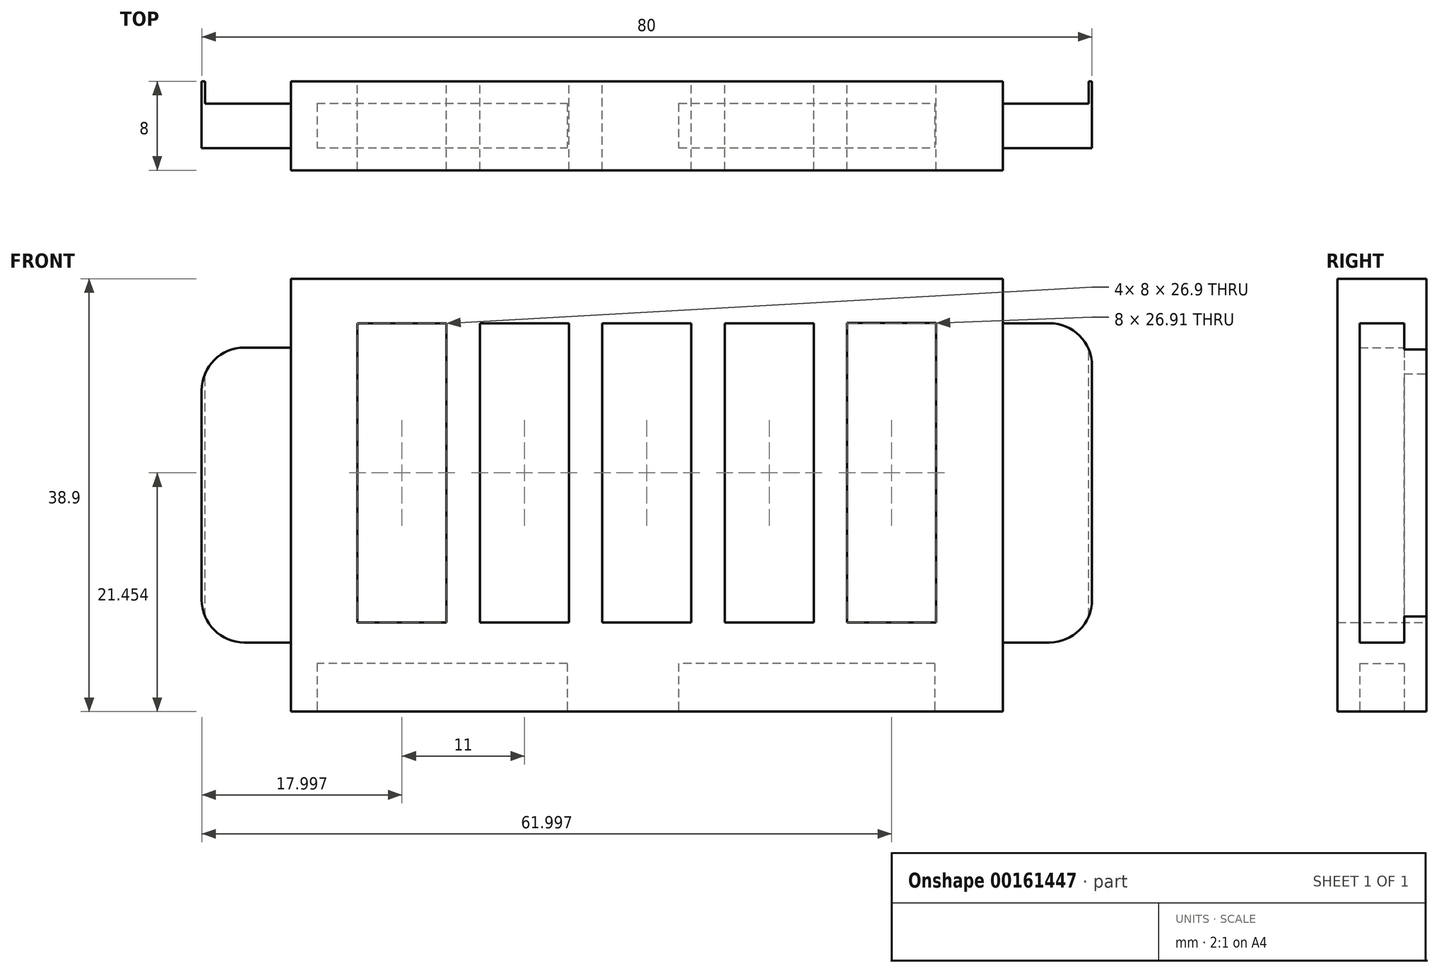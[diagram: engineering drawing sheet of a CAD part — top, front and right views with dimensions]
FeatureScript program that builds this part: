
annotation { "Feature Type Name" : "Feature", "Feature Type Description" : "" }
export const myFeature = defineFeature(function(context is Context, id is Id, definition is map)
    precondition{}
    {
        {
            var Q0;
            Q0=qCreatedBy(makeId("Front.planeOp"),FACE);
            var sketch = newSketch(context, id + "F0", { "sketchPlane" : qUnion([Q0])});
            skLineSegment(sketch, "E0.bottom", {"start": v(-77.72, 39.57) * mm, "end": v(-71.72, 39.57) * mm});
            skLineSegment(sketch, "E0.left", {"start": v(-77.72, 39.57) * mm, "end": v(-77.72, 0.67) * mm});
            skLineSegment(sketch, "E0.right", {"start": v(-13.72, 39.57) * mm, "end": v(-13.72, 0.67) * mm});
            skLineSegment(sketch, "E1.left", {"start": v(-77.72, 0.67) * mm, "end": v(-77.72, 15.56) * mm});
            skLineSegment(sketch, "E1.right", {"start": v(-85.72, 10.7) * mm, "end": v(-85.72, 29.54) * mm});
            skLineSegment(sketch, "E2.top", {"start": v(-77.72, 6.87) * mm, "end": v(-81.89, 6.87) * mm});
            skLineSegment(sketch, "E2.left", {"start": v(-77.72, 0.67) * mm, "end": v(-77.72, 6.87) * mm});
            skLineSegment(sketch, "E3.top", {"start": v(-81.89, 33.37) * mm, "end": v(-77.72, 33.37) * mm});
            skLineSegment(sketch, "E3.right", {"start": v(-77.72, 33.37) * mm, "end": v(-77.72, 15.56) * mm});
            skLineSegment(sketch, "E4.bottom", {"start": v(-13.72, 6.87) * mm, "end": v(-9.56, 6.87) * mm});
            skLineSegment(sketch, "E4.top", {"start": v(-13.72, 35.57) * mm, "end": v(-9.56, 35.57) * mm});
            skLineSegment(sketch, "E4.left", {"start": v(-13.72, 6.87) * mm, "end": v(-13.72, 35.57) * mm});
            skLineSegment(sketch, "E4.right", {"start": v(-5.72, 10.7) * mm, "end": v(-5.72, 31.74) * mm});
            skArc(sketch, "E5.filletArc", {"start": v(-5.72, 31.74) * mm, "mid": v(-6.85, 34.45) * mm, "end": v(-9.56, 35.57) * mm});
            skPoint(sketch, "E6.visualSharp", {"position": v(-5.72, 6.87) * mm});
            skArc(sketch, "E6.filletArc", {"start": v(-9.56, 6.87) * mm, "mid": v(-6.85, 8) * mm, "end": v(-5.72, 10.7) * mm});
            skArc(sketch, "E7.filletArc", {"start": v(-81.89, 33.37) * mm, "mid": v(-84.6, 32.25) * mm, "end": v(-85.72, 29.54) * mm});
            skPoint(sketch, "E8.visualSharp", {"position": v(-85.72, 6.87) * mm});
            skArc(sketch, "E8.filletArc", {"start": v(-85.72, 10.7) * mm, "mid": v(-84.6, 8) * mm, "end": v(-81.89, 6.87) * mm});
            skLineSegment(sketch, "E9.top", {"start": v(-77.72, 0.67) * mm, "end": v(-71.72, 0.67) * mm});
            skLineSegment(sketch, "E9.right", {"start": v(-71.72, 35.57) * mm, "end": v(-71.72, 8.67) * mm});
            skLineSegment(sketch, "E10.bottom", {"start": v(-13.72, 39.57) * mm, "end": v(-21.72, 39.57) * mm});
            skLineSegment(sketch, "E10.left", {"start": v(-13.72, 39.57) * mm, "end": v(-13.72, 0.57) * mm});
            skLineSegment(sketch, "E11.bottom", {"start": v(-71.72, 8.67) * mm, "end": v(-63.72, 8.67) * mm});
            skLineSegment(sketch, "E11.left", {"start": v(-77.72, 8.67) * mm, "end": v(-77.72, 0.67) * mm});
            skLineSegment(sketch, "E11.right", {"start": v(-13.72, 8.67) * mm, "end": v(-13.72, 0.67) * mm});
            skLineSegment(sketch, "E12.top", {"start": v(-71.72, 35.57) * mm, "end": v(-63.72, 35.57) * mm});
            skLineSegment(sketch, "E12.left", {"start": v(-77.72, 39.57) * mm, "end": v(-77.72, 35.57) * mm});
            skLineSegment(sketch, "E12.right", {"start": v(-13.72, 39.57) * mm, "end": v(-13.72, 35.57) * mm});
            skLineSegment(sketch, "E13", {"start": v(-63.72, 35.57) * mm, "end": v(-63.72, 8.67) * mm});
            skLineSegment(sketch, "E14", {"start": v(-60.72, 35.57) * mm, "end": v(-60.72, 8.67) * mm});
            skLineSegment(sketch, "E15", {"start": v(-52.72, 35.57) * mm, "end": v(-52.72, 8.67) * mm});
            skLineSegment(sketch, "E16", {"start": v(-49.72, 35.57) * mm, "end": v(-49.72, 8.67) * mm});
            skLineSegment(sketch, "E17", {"start": v(-41.72, 35.57) * mm, "end": v(-41.72, 8.67) * mm});
            skLineSegment(sketch, "E18.right", {"start": v(-38.72, 35.57) * mm, "end": v(-38.72, 8.67) * mm});
            skLineSegment(sketch, "E19.left", {"start": v(-30.72, 35.57) * mm, "end": v(-30.72, 8.67) * mm});
            skLineSegment(sketch, "E20.trimOffspring", {"start": v(-38.72, 35.57) * mm, "end": v(-30.72, 35.57) * mm});
            skLineSegment(sketch, "E21.trimOffspring", {"start": v(-49.72, 35.57) * mm, "end": v(-41.72, 35.57) * mm});
            skLineSegment(sketch, "E22.trimOffspring", {"start": v(-60.72, 8.67) * mm, "end": v(-52.72, 8.67) * mm});
            skLineSegment(sketch, "E23.trimOffspring", {"start": v(-60.72, 35.57) * mm, "end": v(-52.72, 35.57) * mm});
            skLineSegment(sketch, "E24.trimOffspring", {"start": v(-49.72, 8.67) * mm, "end": v(-41.72, 8.67) * mm});
            skLineSegment(sketch, "E25.trimOffspring", {"start": v(-38.72, 8.67) * mm, "end": v(-30.72, 8.67) * mm});
            skLineSegment(sketch, "E26", {"start": v(-6.02, 9.22) * mm, "end": v(-6.02, 33.23) * mm});
            skLineSegment(sketch, "E27", {"start": v(-85.42, 9.22) * mm, "end": v(-85.42, 31.03) * mm});
            skLineSegment(sketch, "E28.trimOffspring", {"start": v(-21.72, 39.57) * mm, "end": v(-13.72, 39.57) * mm});
            skLineSegment(sketch, "E29", {"start": v(-13.72, 0.67) * mm, "end": v(-71.72, 0.67) * mm});
            skLineSegment(sketch, "E30", {"start": v(-21.72, 39.57) * mm, "end": v(-71.72, 39.57) * mm});
            skLineSegment(sketch, "E31.bottom", {"start": v(-27.72, 35.58) * mm, "end": v(-19.72, 35.58) * mm});
            skLineSegment(sketch, "E31.top", {"start": v(-27.72, 8.67) * mm, "end": v(-19.72, 8.67) * mm});
            skLineSegment(sketch, "E31.left", {"start": v(-27.72, 35.58) * mm, "end": v(-27.72, 8.67) * mm});
            skLineSegment(sketch, "E31.right", {"start": v(-19.72, 35.58) * mm, "end": v(-19.72, 8.67) * mm});
            skSolve(sketch);
        }
        {
            var Q0;
            {var subQ4=sQuery(id+"F0.wireOp",EDGE,"E1.right");Q0=makeQuery(id+"F0.imprint","IMPRINT",FACE,{"disambiguationData":[TD([[makeQuery(id+"F0.imprint","IMPRINT",EDGE,{"derivedFrom":subQ4}),-1.0]])]});}
            var Q1;
            {var subQ1=sQuery(id+"F0.wireOp",EDGE,"E4.right");Q1=makeQuery(id+"F0.imprint","IMPRINT",FACE,{"disambiguationData":[TD([[makeQuery(id+"F0.imprint","IMPRINT",EDGE,{"derivedFrom":subQ1}),1.0]])]});}
            var Q2;
            {var subQ1=sQuery(id+"F0.wireOp",EDGE,"E4.bottom");Q2=makeQuery(id+"F0.imprint","IMPRINT",FACE,{"disambiguationData":[TD([[makeQuery(id+"F0.imprint","IMPRINT",EDGE,{"derivedFrom":subQ1}),1.0]])]});}
            var Q3;
            Q3=makeQuery(id+"F0.imprint","IMPRINT",FACE,{"disambiguationData":[TD([[makeQuery(id+"F0.imprint","IMPRINT",EDGE,{"derivedFrom":sQuery(id+"F0.wireOp",EDGE,"E9.right")}),-1.0]])]});
            var Q4;
            {var subQ1=sQuery(id+"F0.wireOp",EDGE,"E2.top");Q4=makeQuery(id+"F0.imprint","IMPRINT",FACE,{"disambiguationData":[TD([[makeQuery(id+"F0.imprint","IMPRINT",EDGE,{"derivedFrom":subQ1}),-1.0]])]});}
            extrude(context, id + "F1", {"entities" : qUnion([Q0, Q1, Q2, Q3, Q4]), "depth" : 6 * mm});
        }
        {
            var Q0;
            {var subQ1=sQuery(id+"F0.wireOp",EDGE,"E2.top");Q0=makeQuery(id+"F0.imprint","IMPRINT",FACE,{"disambiguationData":[TD([[makeQuery(id+"F0.imprint","IMPRINT",EDGE,{"derivedFrom":subQ1}),-1.0]])]});}
            var Q1;
            {var subQ1=sQuery(id+"F0.wireOp",EDGE,"E4.bottom");Q1=makeQuery(id+"F0.imprint","IMPRINT",FACE,{"disambiguationData":[TD([[makeQuery(id+"F0.imprint","IMPRINT",EDGE,{"derivedFrom":subQ1}),1.0]])]});}
            extrude(context, id + "F2", {"entities" : qUnion([Q0, Q1]), "operationType" : NewBodyOperationType.REMOVE, "depth" : 2 * mm});
        }
        {
            var Q0;
            Q0=makeQuery(id+"F0.imprint","IMPRINT",FACE,{"disambiguationData":[TD([[makeQuery(id+"F0.imprint","IMPRINT",EDGE,{"derivedFrom":sQuery(id+"F0.wireOp",EDGE,"E9.right")}),-1.0]])]});
            extrude(context, id + "F3", {"entities" : qUnion([Q0]), "operationType" : NewBodyOperationType.ADD, "depth" : 8 * mm});
        }
        {
            var Q0;
            Q0=qCreatedBy(makeId("Top.planeOp"),FACE);
            var sketch = newSketch(context, id + "F4", { "sketchPlane" : qUnion([Q0])});
            skLineSegment(sketch, "E32.bottom", {"start": v(67.63, -6) * mm, "end": v(12.13, -6) * mm});
            skLineSegment(sketch, "E32.top", {"start": v(67.63, -2) * mm, "end": v(12.13, -2) * mm});
            skLineSegment(sketch, "E32.left", {"start": v(67.63, -6) * mm, "end": v(67.63, -2) * mm});
            skLineSegment(sketch, "E32.right", {"start": v(-75.37, -6) * mm, "end": v(-75.37, -2) * mm});
            skLineSegment(sketch, "E33", {"start": v(45.13, -6) * mm, "end": v(45.13, -2) * mm});
            skLineSegment(sketch, "E34", {"start": v(-52.87, -6) * mm, "end": v(-52.87, -2) * mm});
            skLineSegment(sketch, "E35", {"start": v(-52.87, -2) * mm, "end": v(-52.87, -4) * mm});
            skLineSegment(sketch, "E36", {"start": v(-42.87, -6) * mm, "end": v(-42.87, -2) * mm});
            skLineSegment(sketch, "E37", {"start": v(35.13, -6) * mm, "end": v(35.13, -2) * mm});
            skLineSegment(sketch, "E38", {"start": v(12.13, -6) * mm, "end": v(12.13, -2) * mm});
            skLineSegment(sketch, "E39", {"start": v(-19.87, -6) * mm, "end": v(-19.87, -2) * mm});
            skLineSegment(sketch, "E40", {"start": v(-19.87, -2) * mm, "end": v(-19.87, -4) * mm});
            skLineSegment(sketch, "E41.trimOffspring", {"start": v(-19.87, -6) * mm, "end": v(-75.37, -6) * mm});
            skLineSegment(sketch, "E42.trimOffspring", {"start": v(-19.87, -2) * mm, "end": v(-75.37, -2) * mm});
            skSolve(sketch);
        }
        {
            var Q0;
            {var subQ3=sQuery(id+"F4.wireOp",EDGE,"E32.right");Q0=makeQuery(id+"F4.imprint","IMPRINT",FACE,{"disambiguationData":[TD([[makeQuery(id+"F4.imprint","IMPRINT",EDGE,{"derivedFrom":subQ3}),-1.0]])]});}
            var Q1;
            {var subQ1=sQuery(id+"F4.wireOp",EDGE,"E36");Q1=makeQuery(id+"F4.imprint","IMPRINT",FACE,{"disambiguationData":[TD([[makeQuery(id+"F4.imprint","IMPRINT",EDGE,{"derivedFrom":subQ1}),-1.0]])]});}
            var Q2;
            {var subQ2=sQuery(id+"F4.wireOp",EDGE,"E37");Q2=makeQuery(id+"F4.imprint","IMPRINT",FACE,{"disambiguationData":[TD([[makeQuery(id+"F4.imprint","IMPRINT",EDGE,{"derivedFrom":subQ2}),1.0]])]});}
            var Q3;
            {var subQ0=sQuery(id+"F4.wireOp",EDGE,"E32.left");Q3=makeQuery(id+"F4.imprint","IMPRINT",FACE,{"disambiguationData":[TD([[makeQuery(id+"F4.imprint","IMPRINT",EDGE,{"derivedFrom":subQ0}),1.0]])]});}
            extrude(context, id + "F5", {"entities" : qUnion([Q0, Q1, Q2, Q3]), "operationType" : NewBodyOperationType.REMOVE, "depth" : 5 * mm});
        }
    });
